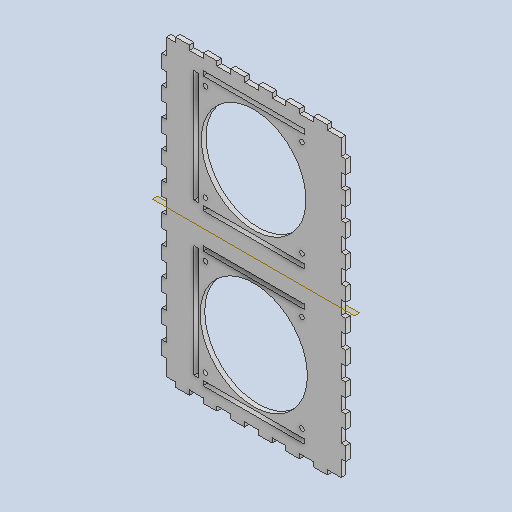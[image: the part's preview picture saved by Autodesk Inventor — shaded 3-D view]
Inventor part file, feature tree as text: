
AUTODESK INVENTOR PART (.ipt)
format: ipt  version: 2023 (Build 270158000, 158)  size: 414,208 bytes
history: native  units: mm
features: reference x24, other x9, extrude x6, sketch x6, plane x1, mirror x1
ambient origin geometry x8: Origin, YZ Plane, XZ Plane, XY Plane, X Axis, Y Axis, Z Axis, Center Point
bodies: Solid1 (feature_tree)
feature tree (47):
  other  "<userpath>\OneDrive\ClawdDrive\Objet3D\Clawd4\parameters.xlsx"
  extrude  "Extrusion1"  Depth=330.0mm
  extrude  "Extrusion2"  TaperAngle=0.0deg  [1 undecoded]
  extrude  "Extrusion3"  Depth=5.0mm
  extrude  "Extrusion4"  Depth=22.5mm
  extrude  "Extrusion5"  Depth=15.0mm
  extrude  "Extrusion6"  Depth=90.0mm
  plane  "Work Plane1"
  mirror  "Mirror1"
  sketch  "Sketch1"  dims[d0=200.0mm d1=330.0mm]
  sketch  "Sketch2"  dims[d2=5.0mm d3=0.0mm]
  sketch  "Sketch3"  dims[d4=0.0mm d5=5.0mm]
  sketch  "Sketch4"  dims[d6=0.0mm d7=22.5mm]
  reference  "Reference1"
  reference  "Reference2"
  reference  "Reference3"
  reference  "Reference4"
  reference  "Reference5"
  reference  "Reference6"
  reference  "Reference7"
  reference  "Reference8"
  reference  "Reference9"
  reference  "Reference10"
  reference  "Reference11"
  reference  "Reference12"
  reference  "Reference13"
  reference  "Reference14"
  reference  "Reference15"
  reference  "Reference16"
  sketch  "Sketch5"  dims[d8=5.0mm d9=15.0mm]
  reference  "Reference17"
  reference  "Reference18"
  reference  "Reference19"
  reference  "Reference20"
  reference  "Reference21"
  reference  "Reference22"
  reference  "Reference23"
  reference  "Reference24"
  sketch  "Sketch6"  dims[d10=15.0mm d11=90.0mm d13=30.0mm d14=10.0mm d16=10.0mm d18=22.5mm d19=5.0mm d20=20.0mm d21=0.0mm d22=5.0mm d23=5.0mm d24=5.0mm d25=5.0mm d26=5.0mm d27=5.0mm d28=5.0mm d29=5.0mm d30=105.0mm d31=105.0mm d32=105.0mm d33=42.5mm d34=190.0mm d35=105.0mm d36=105.0mm d37=105.0mm d38=30.0mm d39=42.5mm d40=30.0mm d41=105.0mm d42=20.0mm d43=0.0mm d47=95.0mm d48=95.0mm d51=30.0mm d52=52.5mm d53=52.5mm d54=10.0mm d55=0.0mm d56=10.0mm d57=0.0mm d58=5.0mm d59=15.0mm d60=70.0mm d62=30.0mm d63=10.0mm d65=10.0mm d67=10.0mm d68=0.0mm]
  other  "<userpath>\OneDrive\ClawdDrive\Objet3D\Clawd4\Assembly1.iam"
  other  "Assembly1.iam"
  other  "FanVerticalPlate:4"
  other  "FanVerticalPlate:3"
  other  "FanVerticalPlate:2"
  other  "FanVerticalPlate:1"
  other  "FANsuport:2"
  other  "FANsuport:1"
note: 1 required parameter value undecoded (feature->parameter linkage not recoverable at this tier; creation-order binding heuristic only, values carry confidence <= 0.55)
